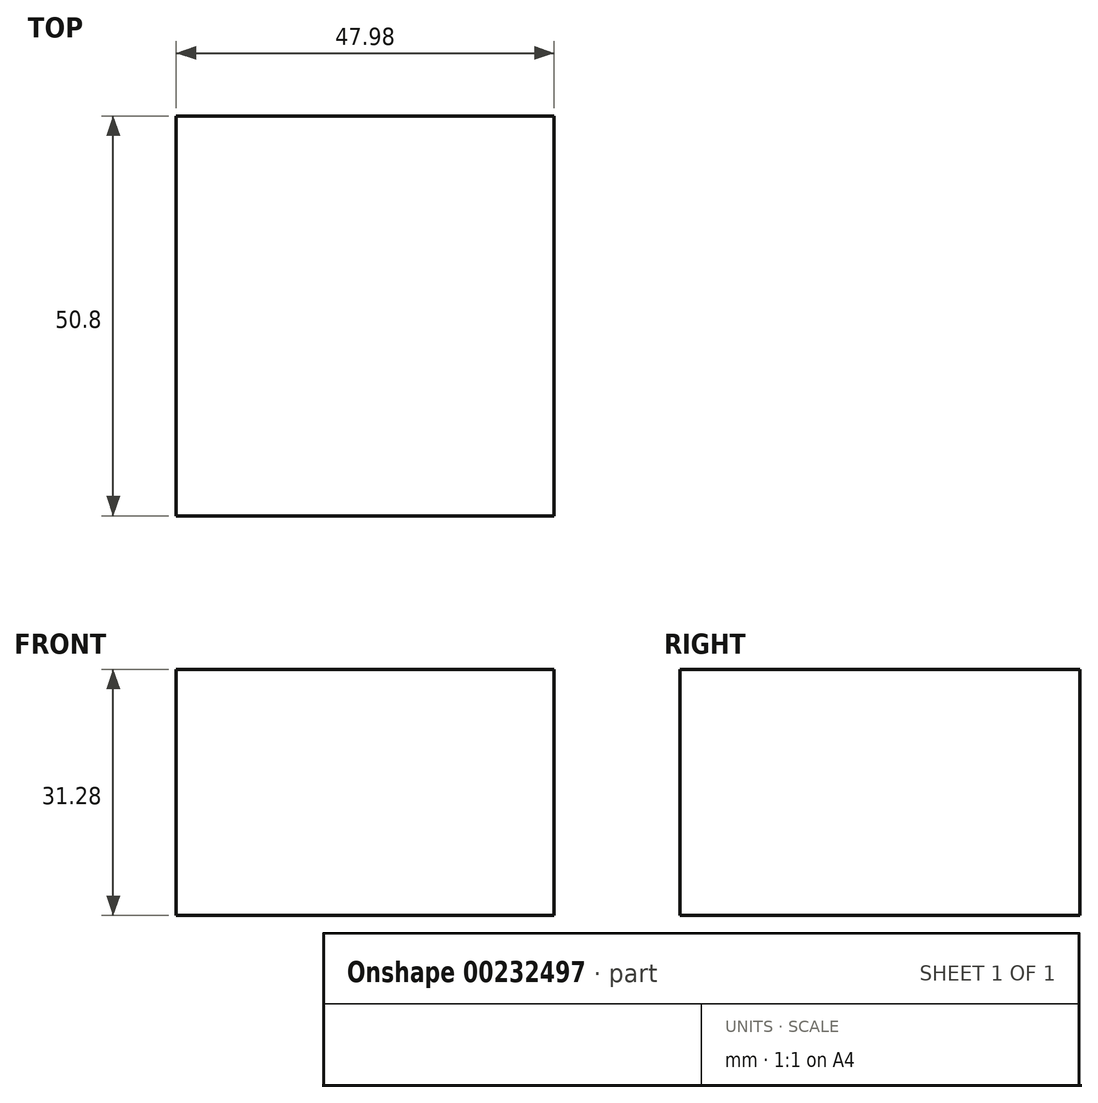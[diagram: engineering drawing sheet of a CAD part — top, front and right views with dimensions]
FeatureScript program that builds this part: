
annotation { "Feature Type Name" : "Feature", "Feature Type Description" : "" }
export const myFeature = defineFeature(function(context is Context, id is Id, definition is map)
    precondition{}
    {
        {
            var Q0;
            Q0=qCreatedBy(makeId("Front.planeOp"),FACE);
            var sketch = newSketch(context, id + "F0", { "sketchPlane" : qUnion([Q0])});
            skLineSegment(sketch, "E0.bottom", {"start": v(-46.92, 41.31) * mm, "end": v(1.06, 41.31) * mm});
            skLineSegment(sketch, "E0.top", {"start": v(-46.92, 10.03) * mm, "end": v(1.06, 10.03) * mm});
            skLineSegment(sketch, "E0.left", {"start": v(-46.92, 41.31) * mm, "end": v(-46.92, 10.03) * mm});
            skLineSegment(sketch, "E0.right", {"start": v(1.06, 41.31) * mm, "end": v(1.06, 10.03) * mm});
            skPoint(sketch, "E0.middle", {"position": v(-22.93, 25.67) * mm});
            skSolve(sketch);
        }
        {
            var Q0;
            Q0 = qSketchRegion(id + "F0", true);
            extrude(context, id + "F1", {"entities" : qUnion([Q0]), "depth" : 50.8 * mm});
        }
    });
